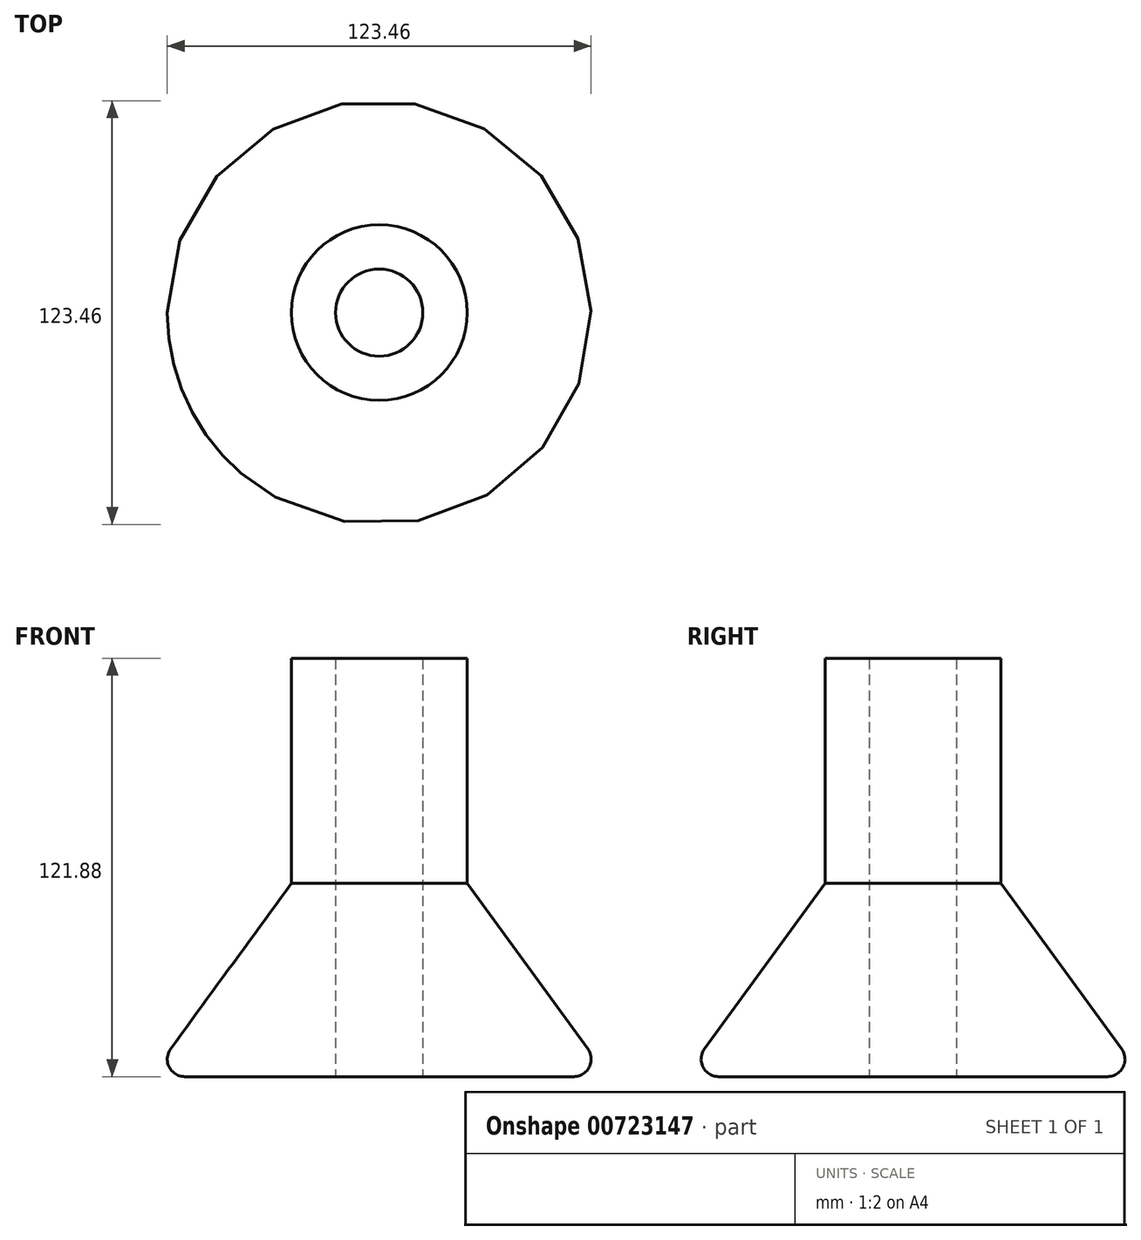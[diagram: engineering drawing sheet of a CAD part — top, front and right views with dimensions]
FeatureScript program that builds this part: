
annotation { "Feature Type Name" : "Feature", "Feature Type Description" : "" }
export const myFeature = defineFeature(function(context is Context, id is Id, definition is map)
    precondition{}
    {
        {
            var Q0;
            Q0=qCreatedBy(makeId("Front.planeOp"),FACE);
            var sketch = newSketch(context, id + "F0", { "sketchPlane" : qUnion([Q0])});
            skLineSegment(sketch, "E0", {"start": v(66.64, -45.96) * mm, "end": v(25.58, 10.36) * mm});
            skLineSegment(sketch, "E1", {"start": v(0, 75.58) * mm, "end": v(0, -45.96) * mm});
            skLineSegment(sketch, "E2", {"start": v(66.64, -45.96) * mm, "end": v(0, -45.96) * mm});
            skLineSegment(sketch, "E3", {"start": v(25.58, 10.36) * mm, "end": v(25.58, 75.92) * mm});
            skLineSegment(sketch, "E4", {"start": v(0, 75.58) * mm, "end": v(25.58, 75.92) * mm});
            skSolve(sketch);
        }
        {
            var Q0;
            Q0 = qSketchRegion(id + "F0", true);
            var Q1;
            Q1=sQuery(id+"F0.wireOp",EDGE,"E1");
            revolve(context, id + "F1", {"surfaceOperationType" : NewSurfaceOperationType.NEW, "entities" : qUnion([Q0]), "axis" : qUnion([Q1]), "revolveType" : RevolveType.FULL});
        }
        {
            var Q0;
            Q0=qCreatedBy(makeId("Top.planeOp"),FACE);
            var sketch = newSketch(context, id + "F2", { "sketchPlane" : qUnion([Q0])});
            skCircle(sketch, "E5", {"center": v(0, 0) * mm, "radius": 12.7 * mm});
            skSolve(sketch);
        }
        {
            var Q0;
            Q0 = qSketchRegion(id + "F2", true);
            extrude(context, id + "F3", {"entities" : qUnion([Q0]), "operationType" : NewBodyOperationType.REMOVE, "endBound" : BoundingType.SYMMETRIC, "depth" : 152.4 * mm, "offsetDistance" : 25.4 * mm});
        }
        {
            var Q0;
            Q0=makeQuery(id+"F1.opRevolve","SWEPT_EDGE",EDGE,{"disambiguationData":[OSD([sQuery(id+"F0.wireOp",EDGE,"E0"),sQuery(id+"F0.wireOp",EDGE,"E2")])]});
            var Q1;
            Q1=makeQuery(id+"F1.opRevolve","SWEPT_EDGE",EDGE,{"disambiguationData":[OSD([sQuery(id+"F0.wireOp",EDGE,"zp0eNZYT-1Ace-icCE-SN76-JCn3LpcDsurJ"),sQuery(id+"F0.wireOp",EDGE,"2uxntvn7-6BVK-3p3u-nsmJ-ptwqOMEJRdvM")])]});
            fillet(context, id + "F4", {"entities" : qUnion([Q0, Q1]), "radius" : 5.08 * mm, "tangentPropagation" : true, "allowEdgeOverflow" : false});
        }
    });
